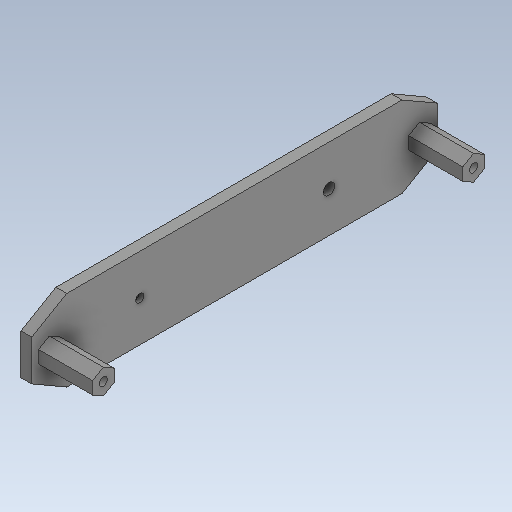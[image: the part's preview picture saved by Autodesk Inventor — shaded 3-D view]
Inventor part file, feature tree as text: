
AUTODESK INVENTOR PART (.ipt)
format: ipt  version: 2020 (Build 240168000, 168)  size: 236,544 bytes
history: native  units: in
note: dims shown in document units (in); Inventor stores cm internally (conversion verified against a paired STEP export)
features: extrude x7, sketch x7, plane x1
ambient origin geometry x8: Origin, YZ Plane, XZ Plane, XY Plane, X Axis, Y Axis, Z Axis, Center Point
bodies: Solid1 (feature_tree)
feature tree (15):
  extrude  "Extrusion1"  Depth=5.9055in
  extrude  "Extrusion3"  TaperAngle=0.0deg  [1 undecoded]
  extrude  "Extrusion4"  Depth=0.7874in
  plane  "Work Plane1"
  extrude  "Extrusion5"  Depth=0.122in
  extrude  "Extrusion6"  Depth=0.2402in
  extrude  "Extrusion7"  [1 undecoded]
  extrude  "Extrusion8"  Depth=0.0866in TaperAngle=0.0deg
  sketch  "Sketch1"  dims[d0=1.1811in d1=5.9055in]
  sketch  "Sketch2"  dims[d2=0.1575in d3=0.0in]
  sketch  "Sketch3"  dims[d8=0.315in d9=0.7874in]
  sketch  "Sketch4"  dims[d10=0.0in d12=0.122in]
  sketch  "Sketch5"  dims[d13=0.0in d14=0.0in d15=0.2402in]
  sketch  "Sketch8"  dims[d16=0.0866in d17=-0.2233in]
  sketch  "Sketch9"  dims[d18=-0.3937in d19=0.0866in d20=0.0in d26=1.5748in d27=0.1654in d28=0.122in d29=1.5748in d30=0.0in d31=0.0in d32=0.2402in d33=0.0866in d34=-0.2233in]
note: 2 required parameter values undecoded (feature->parameter linkage not recoverable at this tier; creation-order binding heuristic only, values carry confidence <= 0.55)
